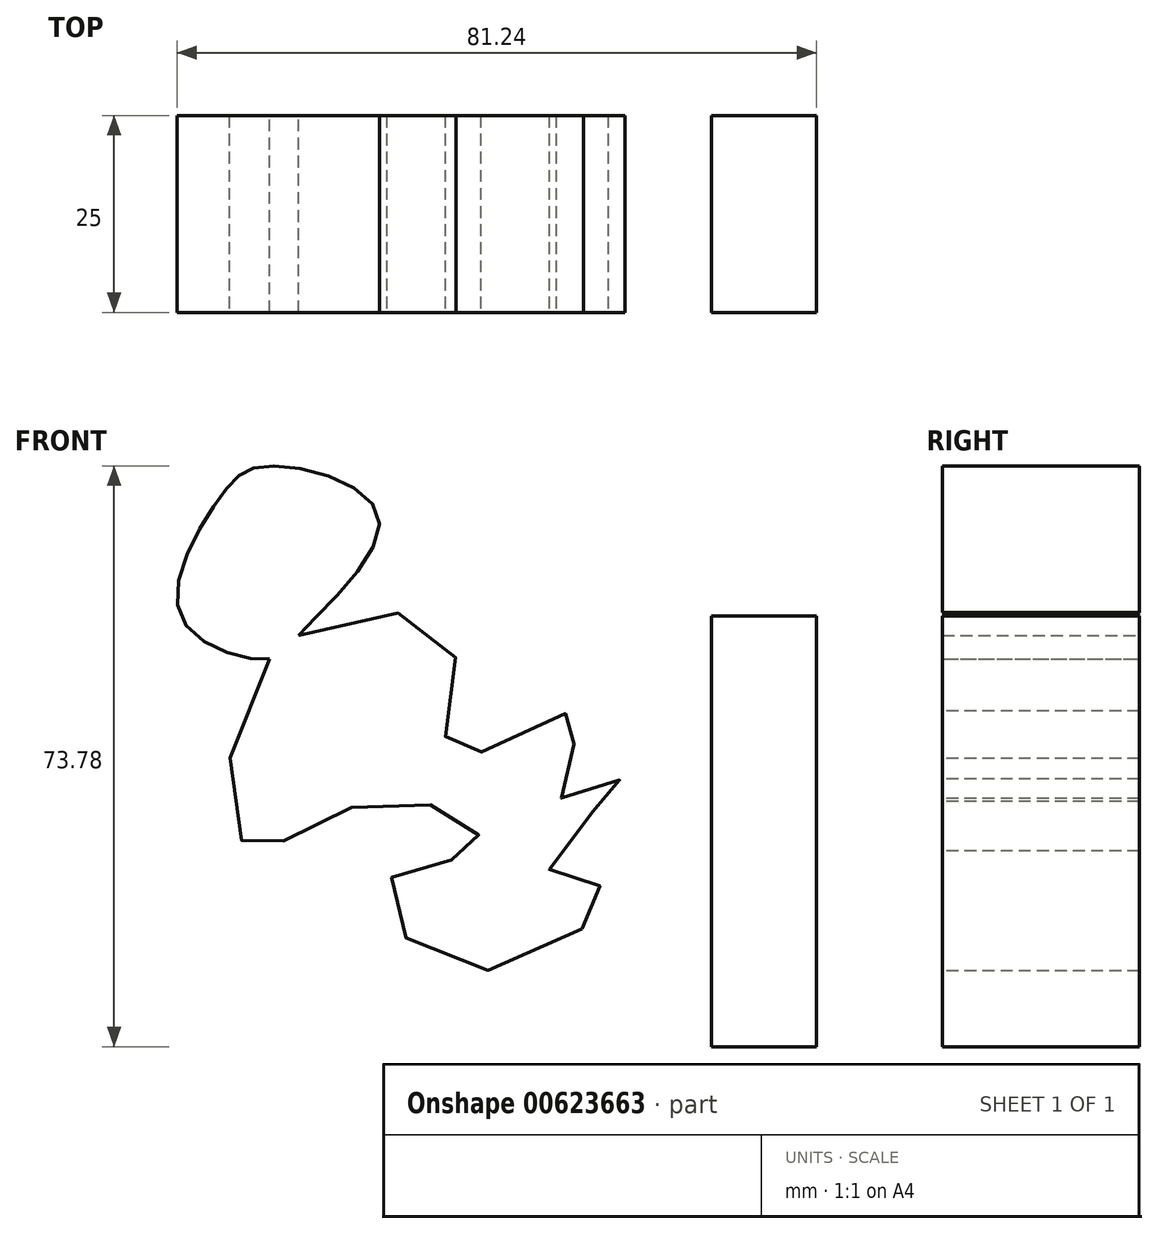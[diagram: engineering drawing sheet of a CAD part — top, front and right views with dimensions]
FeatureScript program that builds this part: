
annotation { "Feature Type Name" : "Feature", "Feature Type Description" : "" }
export const myFeature = defineFeature(function(context is Context, id is Id, definition is map)
    precondition{}
    {
        {
            var Q0;
            Q0=qCreatedBy(makeId("Front.planeOp"),FACE);
            var sketch = newSketch(context, id + "F0", { "sketchPlane" : qUnion([Q0])});
            skLineSegment(sketch, "E0.bottom", {"start": v(0, 0) * mm, "end": v(13.37, 0) * mm});
            skLineSegment(sketch, "E0.top", {"start": v(0, 54.69) * mm, "end": v(13.37, 54.69) * mm});
            skLineSegment(sketch, "E0.left", {"start": v(0, 0) * mm, "end": v(0, 54.69) * mm});
            skLineSegment(sketch, "E0.right", {"start": v(13.37, 0) * mm, "end": v(13.37, 54.69) * mm});
            skFitSpline(sketch, "E1", {"points": [v(-32.97, 51.14) * mm, v(-32.97, 36.69) * mm, v(-16.38, 42.41) * mm, v(-19.47, 31.78) * mm, v(-10.98, 33.96) * mm, v(-20.63, 22.78) * mm, v(-13.3, 19.78) * mm, v(-31.43, 9.68) * mm, v(-40.68, 21.41) * mm, v(-29.88, 24.69) * mm, v(-31.43, 29.05) * mm, v(-48.78, 29.32) * mm, v(-58.81, 25.23) * mm, v(-56.11, 49.23) * mm, v(-32.97, 51.14) * mm]});
            skFitSpline(sketch, "E2", {"points": [v(-56.11, 49.23) * mm, v(-67.3, 54.41) * mm, v(-62.67, 69.41) * mm, v(-56.11, 73.78) * mm, v(-42.23, 67.23) * mm, v(-52.44, 52.2) * mm, v(-56.11, 49.23) * mm]});
            skSolve(sketch);
        }
        {
            var Q0;
            Q0 = qSketchRegion(id + "F0", true);
            extrude(context, id + "F1", {"entities" : qUnion([Q0]), "depth" : 25 * mm, "offsetDistance" : 25 * mm});
        }
        {
            var Q0;
            Q0 = qSketchRegion(id + "F0", true);
            extrude(context, id + "F2", {"entities" : qUnion([Q0]), "depth" : 25 * mm, "offsetDistance" : 25 * mm});
        }
    });
